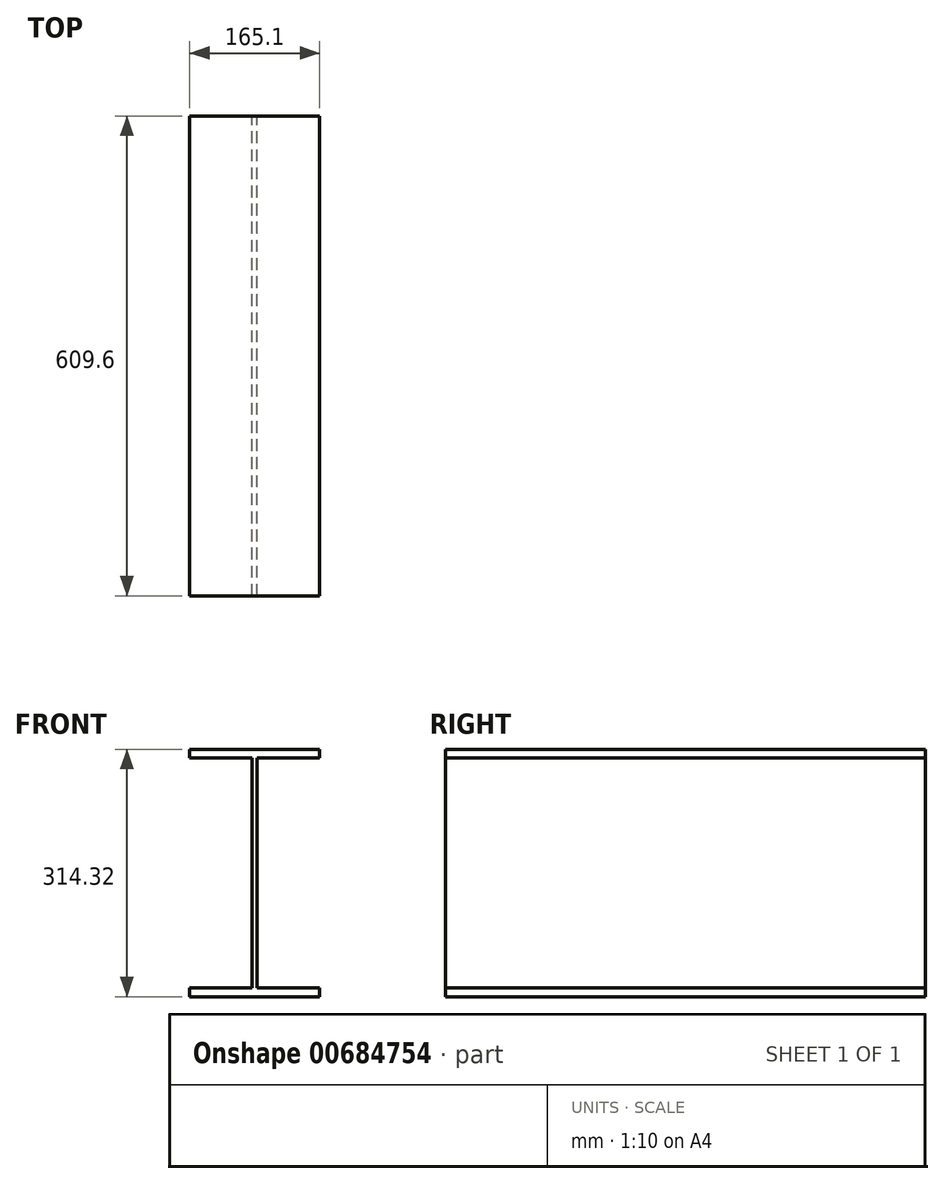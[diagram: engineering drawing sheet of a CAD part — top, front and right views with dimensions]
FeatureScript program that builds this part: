
annotation { "Feature Type Name" : "Feature", "Feature Type Description" : "" }
export const myFeature = defineFeature(function(context is Context, id is Id, definition is map)
    precondition{}
    {
        {
            var Q0;
            Q0=qCreatedBy(makeId("Front.planeOp"),FACE);
            var sketch = newSketch(context, id + "F0", { "sketchPlane" : qUnion([Q0])});
            skLineSegment(sketch, "E0", {"start": v(-82.55, 157.16) * mm, "end": v(82.55, 157.16) * mm});
            skLineSegment(sketch, "E1", {"start": v(82.55, 157.16) * mm, "end": v(82.55, 146.05) * mm});
            skLineSegment(sketch, "E2", {"start": v(82.55, 146.05) * mm, "end": v(3.17, 146.05) * mm});
            skLineSegment(sketch, "E3", {"start": v(3.17, 146.05) * mm, "end": v(3.18, -146.05) * mm});
            skLineSegment(sketch, "E4", {"start": v(3.18, -146.05) * mm, "end": v(82.55, -146.05) * mm});
            skLineSegment(sketch, "E5", {"start": v(-82.55, 157.16) * mm, "end": v(-82.55, 146.05) * mm});
            skLineSegment(sketch, "E6", {"start": v(-82.55, 146.05) * mm, "end": v(-3.18, 146.05) * mm});
            skLineSegment(sketch, "E7", {"start": v(-3.18, 146.05) * mm, "end": v(-3.17, -146.05) * mm});
            skLineSegment(sketch, "E8", {"start": v(-3.17, -146.05) * mm, "end": v(-82.55, -146.05) * mm});
            skLineSegment(sketch, "E9", {"start": v(-82.55, -146.05) * mm, "end": v(-82.55, -157.16) * mm});
            skLineSegment(sketch, "E10", {"start": v(-82.55, -157.16) * mm, "end": v(82.55, -157.16) * mm});
            skLineSegment(sketch, "E11", {"start": v(82.55, -157.16) * mm, "end": v(82.55, -146.05) * mm});
            skLineSegment(sketch, "E12", {"start": v(3.17, 146.05) * mm, "end": v(-3.17, -146.05) * mm, "construction": true});
            skSolve(sketch);
        }
        {
            var Q0;
            Q0=qSketchRegion(id+"F0",true);
            extrude(context, id + "F1", {"entities" : qUnion([Q0]), "depth" : 609.6 * mm, "offsetDistance" : 25.4 * mm});
        }
    });
